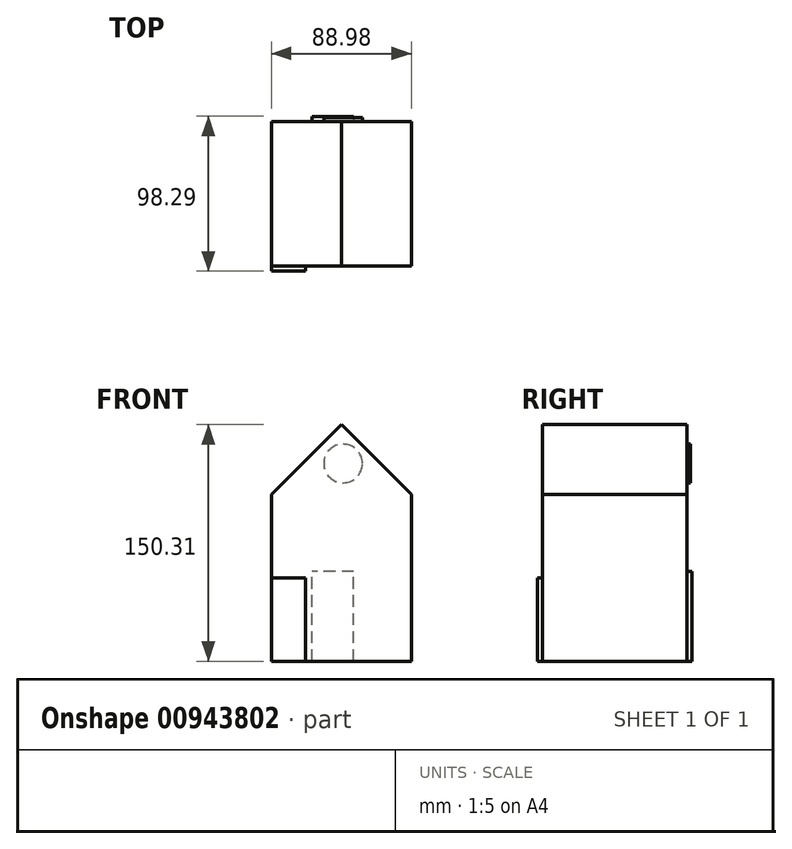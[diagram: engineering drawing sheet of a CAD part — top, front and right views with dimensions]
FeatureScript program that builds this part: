
annotation { "Feature Type Name" : "Feature", "Feature Type Description" : "" }
export const myFeature = defineFeature(function(context is Context, id is Id, definition is map)
    precondition{}
    {
        {
            var Q0;
            Q0=qCreatedBy(makeId("Top.planeOp"),FACE);
            var sketch = newSketch(context, id + "F0", { "sketchPlane" : qUnion([Q0])});
            skLineSegment(sketch, "E0.bottom", {"start": v(-45.6, -43.72) * mm, "end": v(43.37, -43.72) * mm});
            skLineSegment(sketch, "E0.top", {"start": v(-45.6, 48.18) * mm, "end": v(43.37, 48.18) * mm});
            skLineSegment(sketch, "E0.left", {"start": v(-45.6, -43.72) * mm, "end": v(-45.6, 48.18) * mm});
            skLineSegment(sketch, "E0.right", {"start": v(43.37, -43.72) * mm, "end": v(43.37, 48.18) * mm});
            skSolve(sketch);
        }
        {
            var Q0;
            Q0=makeQuery(id+"F0.imprint","IMPRINT",FACE,{"disambiguationData":[TD([[makeQuery(id+"F0.imprint","IMPRINT",EDGE,{"derivedFrom":sQuery(id+"F0.wireOp",EDGE,"E0.bottom")}),1.0]])]});
            extrude(context, id + "F1", {"entities" : qUnion([Q0]), "depth" : 92.02 * mm, "offsetDistance" : 25.4 * mm});
        }
        {
            var Q0;
            Q0=makeQuery(id+"F1.opExtrude","CAP_FACE",FACE,{"disambiguationData":[OSD([sQuery(id+"F0.wireOp",EDGE,"E0.bottom"),sQuery(id+"F0.wireOp",EDGE,"E0.top"),sQuery(id+"F0.wireOp",EDGE,"E0.left"),sQuery(id+"F0.wireOp",EDGE,"E0.right")])],"isStart":false});
            var sketch = newSketch(context, id + "F2", { "sketchPlane" : qUnion([Q0])});
            skLineSegment(sketch, "E1.bottom", {"start": v(-45.6, 48.18) * mm, "end": v(43.37, 48.18) * mm});
            skLineSegment(sketch, "E1.top", {"start": v(-45.6, -43.72) * mm, "end": v(43.37, -43.72) * mm});
            skLineSegment(sketch, "E1.left", {"start": v(-45.6, 48.18) * mm, "end": v(-45.6, -43.72) * mm});
            skLineSegment(sketch, "E1.right", {"start": v(43.37, 48.18) * mm, "end": v(43.37, -43.72) * mm});
            skSolve(sketch);
        }
        {
            var Q0;
            Q0 = qSketchRegion(id + "F2", true);
            extrude(context, id + "F3", {"entities" : qUnion([Q0]), "operationType" : NewBodyOperationType.ADD, "depth" : 64.6 * mm, "offsetDistance" : 25.4 * mm});
        }
        {
            var Q0;
            Q0=makeQuery(id+"F3.opExtrude","CAP_EDGE",EDGE,{"disambiguationData":[OSD([sQuery(id+"F2.wireOp",EDGE,"E1.left")])],"isStart":false});
            var Q1;
            Q1=makeQuery(id+"F3.opExtrude","CAP_EDGE",EDGE,{"disambiguationData":[OSD([sQuery(id+"F2.wireOp",EDGE,"E1.right")])],"isStart":false});
            chamfer(context, id + "F4", {"entities" : qUnion([Q0, Q1]), "width" : 50.8 * mm, "tangentPropagation" : true});
        }
        {
            var Q0;
            Q0=makeQuery(id+"F3.boolean.opBoolean","MERGE",FACE,{"derivedFrom":[makeQuery(id+"F1.opExtrude","SWEPT_FACE",FACE,{"disambiguationData":[OSD([sQuery(id+"F0.wireOp",EDGE,"E0.top")])]}),makeQuery(id+"F3.opExtrude","SWEPT_FACE",FACE,{"disambiguationData":[OSD([sQuery(id+"F2.wireOp",EDGE,"E1.bottom")])]})]});
            var sketch = newSketch(context, id + "F5", { "sketchPlane" : qUnion([Q0])});
            skLineSegment(sketch, "E2", {"start": v(-43.37, 105.82) * mm, "end": v(45.6, 105.82) * mm});
            skLineSegment(sketch, "E3.bottom", {"start": v(-6.66, 0) * mm, "end": v(19.92, 0) * mm});
            skLineSegment(sketch, "E3.top", {"start": v(-6.66, 57.1) * mm, "end": v(19.92, 57.1) * mm});
            skLineSegment(sketch, "E3.left", {"start": v(-6.66, 0) * mm, "end": v(-6.66, 57.1) * mm});
            skLineSegment(sketch, "E3.right", {"start": v(19.92, 0) * mm, "end": v(19.92, 57.1) * mm});
            skSolve(sketch);
        }
        {
            var Q0;
            Q0 = qSketchRegion(id + "F5", true);
            extrude(context, id + "F6", {"entities" : qUnion([Q0]), "operationType" : NewBodyOperationType.ADD, "depth" : 3.3 * mm, "offsetDistance" : 25.4 * mm});
        }
        {
            var Q0;
            Q0=makeQuery(id+"F3.boolean.opBoolean","MERGE",FACE,{"derivedFrom":[makeQuery(id+"F1.opExtrude","SWEPT_FACE",FACE,{"disambiguationData":[OSD([sQuery(id+"F0.wireOp",EDGE,"E0.top")])]}),makeQuery(id+"F3.opExtrude","SWEPT_FACE",FACE,{"disambiguationData":[OSD([sQuery(id+"F2.wireOp",EDGE,"E1.bottom")])]})]});
            var sketch = newSketch(context, id + "F7", { "sketchPlane" : qUnion([Q0])});
            skLineSegment(sketch, "E4", {"start": v(-43.37, 105.82) * mm, "end": v(45.6, 105.82) * mm});
            skSolve(sketch);
        }
        {
            var Q0;
            Q0=makeQuery(id+"F3.boolean.opBoolean","MERGE",FACE,{"derivedFrom":[makeQuery(id+"F1.opExtrude","SWEPT_FACE",FACE,{"disambiguationData":[OSD([sQuery(id+"F0.wireOp",EDGE,"E0.bottom")])]}),makeQuery(id+"F3.opExtrude","SWEPT_FACE",FACE,{"disambiguationData":[OSD([sQuery(id+"F2.wireOp",EDGE,"E1.top")])]})]});
            var sketch = newSketch(context, id + "F8", { "sketchPlane" : qUnion([Q0])});
            skPoint(sketch, "E5.oppositeSnap0", {"position": v(-45.6, 52.9) * mm});
            skLineSegment(sketch, "E5.bottom", {"start": v(-45.6, 0) * mm, "end": v(-23.75, 0) * mm});
            skLineSegment(sketch, "E5.top", {"start": v(-45.6, 52.9) * mm, "end": v(-23.75, 52.9) * mm});
            skLineSegment(sketch, "E5.left", {"start": v(-45.6, 0) * mm, "end": v(-45.6, 52.9) * mm});
            skLineSegment(sketch, "E5.right", {"start": v(-23.75, 0) * mm, "end": v(-23.75, 52.9) * mm});
            skSolve(sketch);
        }
        {
            var Q0;
            Q0 = qSketchRegion(id + "F8", true);
            extrude(context, id + "F9", {"entities" : qUnion([Q0]), "operationType" : NewBodyOperationType.ADD, "depth" : 3.08 * mm, "offsetDistance" : 25.4 * mm});
        }
        {
            var Q0;
            Q0=makeQuery(id+"F7.imprint","IMPRINT",FACE,{"disambiguationData":[TD([[makeQuery(id+"F7.imprint","IMPRINT",EDGE,{"derivedFrom":sQuery(id+"F7.wireOp",EDGE,"E4")}),1.0]])]});
            var sketch = newSketch(context, id + "F10", { "sketchPlane" : qUnion([Q0])});
            skCircle(sketch, "E6", {"center": v(0, 125.6) * mm, "radius": 12.27 * mm});
            skSolve(sketch);
        }
        {
            var Q0;
            Q0 = qSketchRegion(id + "F10", true);
            extrude(context, id + "F11", {"entities" : qUnion([Q0]), "operationType" : NewBodyOperationType.ADD, "depth" : 1.73 * mm, "offsetDistance" : 25.4 * mm});
        }
        {
            var Q0;
            Q0=makeQuery(id+"F11.opExtrude","CAP_FACE",FACE,{"disambiguationData":[OSD([sQuery(id+"F10.wireOp",EDGE,"E6")])],"isStart":false});
            extrude(context, id + "F12", {"entities" : qUnion([Q0]), "operationType" : NewBodyOperationType.ADD, "depth" : 0.65 * mm, "offsetDistance" : 25.4 * mm});
        }
    });
